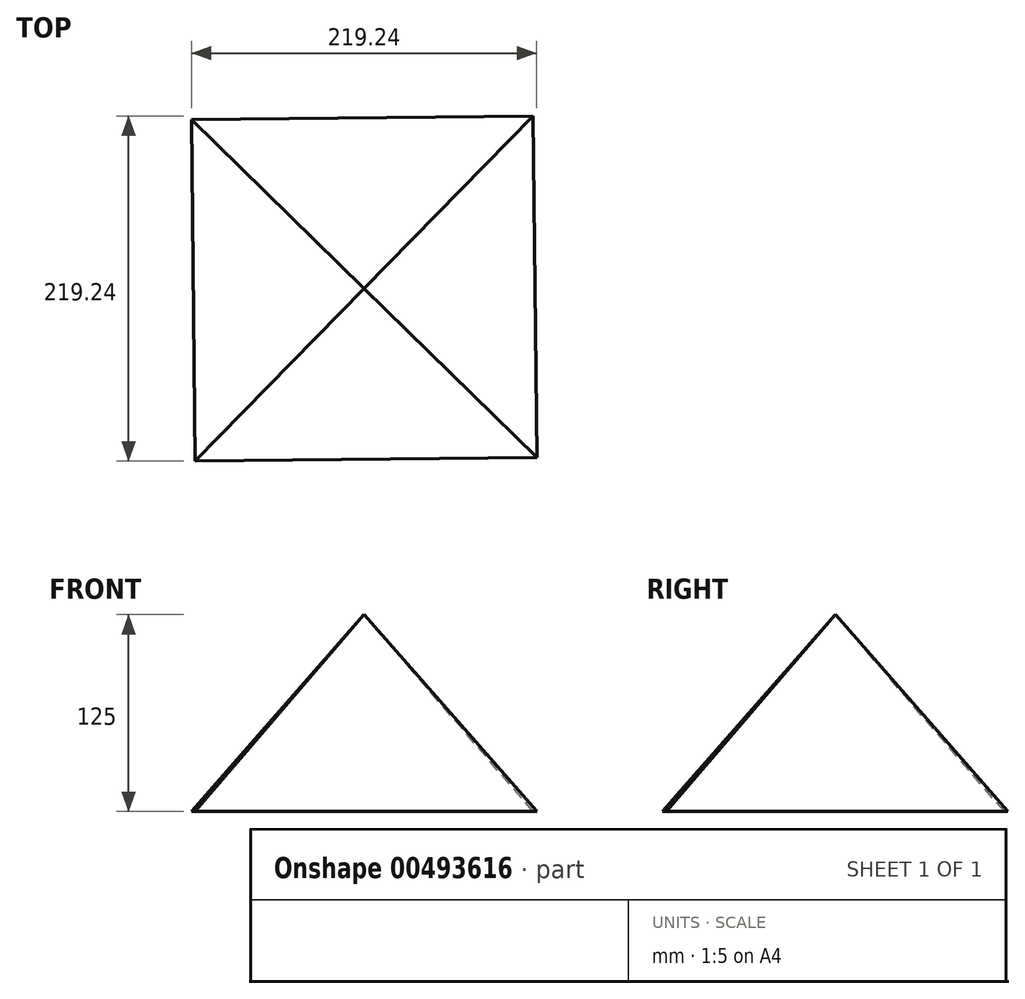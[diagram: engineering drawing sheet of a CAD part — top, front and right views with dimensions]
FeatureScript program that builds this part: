
annotation { "Feature Type Name" : "Feature", "Feature Type Description" : "" }
export const myFeature = defineFeature(function(context is Context, id is Id, definition is map)
    precondition{}
    {
        {
            var Q0;
            Q0=qCreatedBy(makeId("Top.planeOp"),FACE);
            var sketch = newSketch(context, id + "F0", { "sketchPlane" : qUnion([Q0])});
            skCircle(sketch, "E0.cCircle", {"center": v(0, 0) * mm, "radius": 153.4 * mm, "construction": true});
            skLineSegment(sketch, "E0.0", {"start": v(-107.3, -109.62) * mm, "end": v(-109.62, 107.3) * mm});
            skLineSegment(sketch, "E0.1", {"start": v(-109.62, 107.3) * mm, "end": v(107.3, 109.62) * mm});
            skLineSegment(sketch, "E0.2", {"start": v(107.3, 109.62) * mm, "end": v(109.62, -107.3) * mm});
            skLineSegment(sketch, "E0.3", {"start": v(109.62, -107.3) * mm, "end": v(-107.3, -109.62) * mm});
            skSolve(sketch);
        }
        {
            var Q0;
            Q0=qCreatedBy(makeId("Top.planeOp"),FACE);
            cPlane(context, id + "F1", {"entities" : qUnion([Q0]), "cplaneType" : CPlaneType.OFFSET, "offset" : 125 * mm, "width" : 150 * mm, "height" : 150 * mm});
        }
        {
            var Q0;
            Q0=qCreatedBy(id+"F1.planeOp",FACE);
            var sketch = newSketch(context, id + "F2", { "sketchPlane" : qUnion([Q0])});
            skPoint(sketch, "E1", {"position": v(0, 0) * mm});
            skSolve(sketch);
        }
        {
            var Q0;
            Q0=makeQuery(id+"F0.imprint","IMPRINT",FACE,{"disambiguationData":[TD([[makeQuery(id+"F0.imprint","IMPRINT",EDGE,{"derivedFrom":sQuery(id+"F0.wireOp",EDGE,"E0.0")}),-1.0]])]});
            var Q1;
            Q1=sQuery(id+"F2.wireOp",VERTEX,"E1");
            loft(context, id + "F3", {"sheetProfilesArray" : [{ "sheetProfileEntities" : qUnion([Q0]) }, { "sheetProfileEntities" : qUnion([Q1]) }]});
        }
    });
